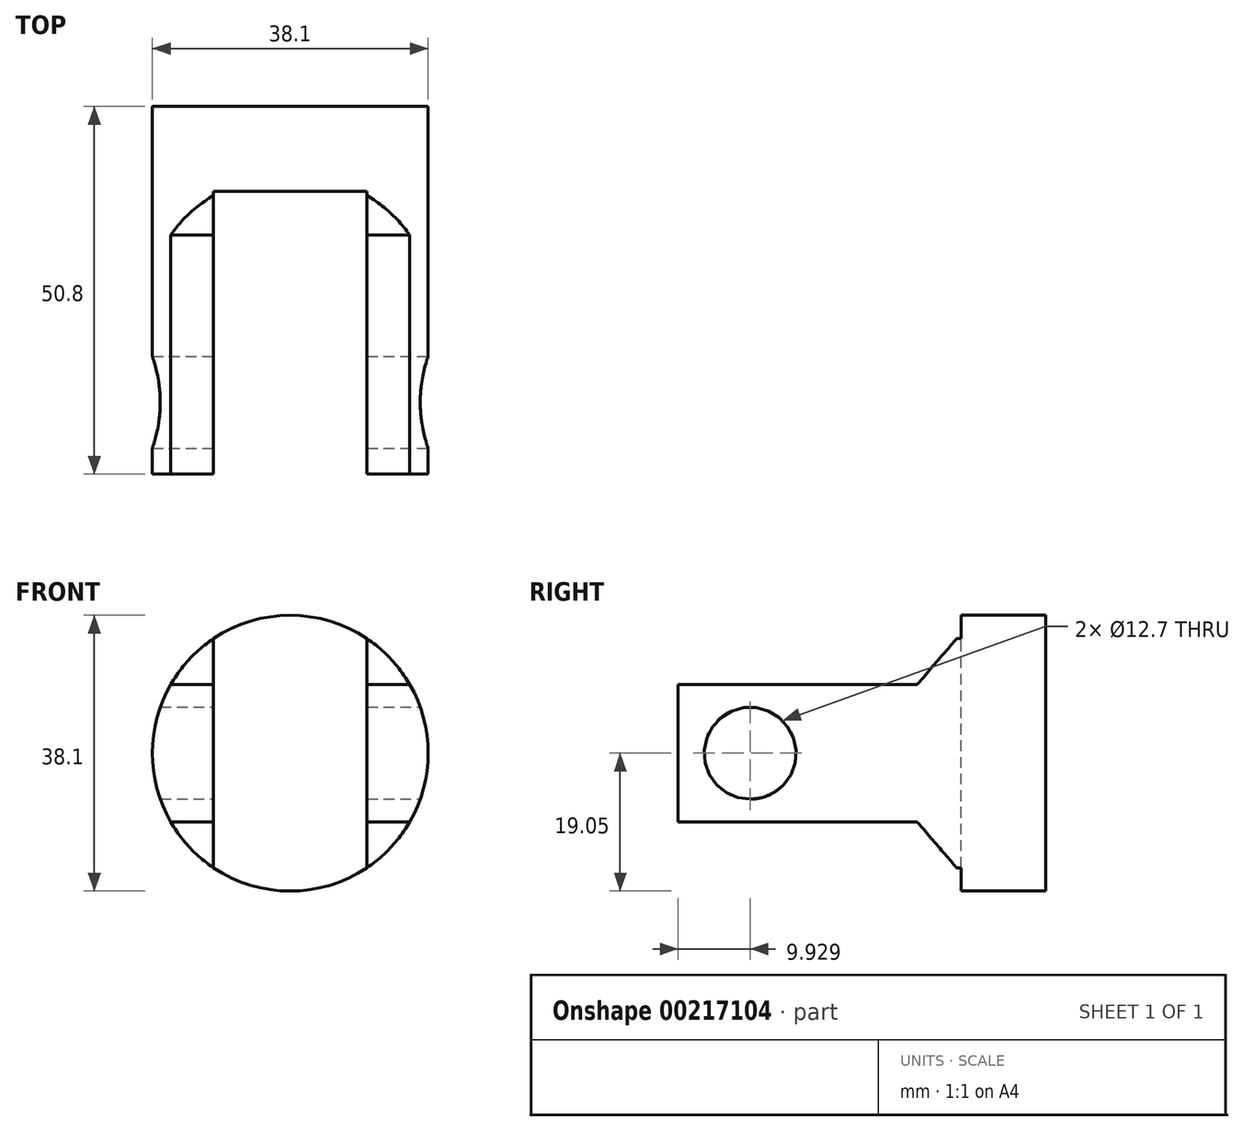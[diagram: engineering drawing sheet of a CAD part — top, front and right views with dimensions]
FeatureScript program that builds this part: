
annotation { "Feature Type Name" : "Feature", "Feature Type Description" : "" }
export const myFeature = defineFeature(function(context is Context, id is Id, definition is map)
    precondition{}
    {
        {
            var Q0;
            Q0=qCreatedBy(makeId("Front.planeOp"),FACE);
            var sketch = newSketch(context, id + "F0", { "sketchPlane" : qUnion([Q0])});
            skCircle(sketch, "E0", {"center": v(0, 0) * mm, "radius": 19.05 * mm});
            skSolve(sketch);
        }
        {
            var Q0;
            Q0 = qSketchRegion(id + "F0", true);
            extrude(context, id + "F1", {"entities" : qUnion([Q0]), "depth" : 50.8 * mm});
        }
        {
            var Q0;
            Q0=qCreatedBy(makeId("Top.planeOp"),FACE);
            var sketch = newSketch(context, id + "F2", { "sketchPlane" : qUnion([Q0])});
            skLineSegment(sketch, "E1.bottom", {"start": v(10.6, -90.36) * mm, "end": v(-10.6, -90.36) * mm});
            skLineSegment(sketch, "E1.top", {"start": v(10.6, -11.7) * mm, "end": v(-10.6, -11.7) * mm});
            skLineSegment(sketch, "E1.left", {"start": v(10.6, -90.36) * mm, "end": v(10.6, -11.7) * mm});
            skLineSegment(sketch, "E1.right", {"start": v(-10.6, -90.36) * mm, "end": v(-10.6, -11.7) * mm});
            skPoint(sketch, "E1.middle", {"position": v(0, -51.03) * mm});
            skSolve(sketch);
        }
        {
            var Q0;
            Q0 = qSketchRegion(id + "F2", true);
            extrude(context, id + "F3", {"entities" : qUnion([Q0]), "operationType" : NewBodyOperationType.REMOVE, "oppositeDirection" : true, "depth" : 76.2 * mm, "symmetric" : true});
        }
        {
            var Q0;
            Q0=qCreatedBy(makeId("Right.planeOp"),FACE);
            var sketch = newSketch(context, id + "F4", { "sketchPlane" : qUnion([Q0])});
            skCircle(sketch, "E2", {"center": v(-40.87, 0) * mm, "radius": 6.35 * mm});
            skLineSegment(sketch, "E3", {"start": v(-54.9, 0) * mm, "end": v(-54.9, -9.5) * mm});
            skLineSegment(sketch, "E4", {"start": v(-54.9, -9.5) * mm, "end": v(-17.78, -9.5) * mm});
            skLineSegment(sketch, "E5", {"start": v(-17.78, -9.5) * mm, "end": v(-12.26, -15.9) * mm});
            skLineSegment(sketch, "E6", {"start": v(-12.26, -15.9) * mm, "end": v(-18.89, -28.72) * mm});
            skLineSegment(sketch, "E7", {"start": v(-18.89, -28.72) * mm, "end": v(-61.3, -20.33) * mm});
            skLineSegment(sketch, "E8", {"start": v(-61.3, -20.33) * mm, "end": v(-54.9, -9.5) * mm});
            skLineSegment(sketch, "E9.MirrorCS", {"start": v(-54.9, 9.5) * mm, "end": v(-17.78, 9.5) * mm});
            skLineSegment(sketch, "E10.MirrorCS", {"start": v(-61.3, 20.33) * mm, "end": v(-54.9, 9.5) * mm});
            skLineSegment(sketch, "E11.MirrorCS", {"start": v(-18.89, 28.72) * mm, "end": v(-61.3, 20.33) * mm});
            skLineSegment(sketch, "E12.MirrorCS", {"start": v(-12.26, 15.9) * mm, "end": v(-18.89, 28.72) * mm});
            skLineSegment(sketch, "E13.MirrorCS", {"start": v(-17.78, 9.5) * mm, "end": v(-12.26, 15.9) * mm});
            skSolve(sketch);
        }
        {
            var Q0;
            Q0=makeQuery(id+"F4.imprint","IMPRINT",FACE,{"disambiguationData":[TD([[makeQuery(id+"F4.imprint","IMPRINT",EDGE,{"derivedFrom":sQuery(id+"F4.wireOp",EDGE,"E2")}),1.0]])]});
            var Q1;
            Q1=makeQuery(id+"F4.imprint","IMPRINT",FACE,{"disambiguationData":[TD([[makeQuery(id+"F4.imprint","IMPRINT",EDGE,{"derivedFrom":sQuery(id+"F4.wireOp",EDGE,"E4")}),-1.0]])]});
            var Q2;
            Q2=makeQuery(id+"F4.imprint","IMPRINT",FACE,{"disambiguationData":[TD([[makeQuery(id+"F4.imprint","IMPRINT",EDGE,{"derivedFrom":sQuery(id+"F4.wireOp",EDGE,"E9.MirrorCS")}),1.0]])]});
            extrude(context, id + "F5", {"entities" : qUnion([Q0, Q1, Q2]), "operationType" : NewBodyOperationType.REMOVE, "oppositeDirection" : true, "depth" : 76.2 * mm, "symmetric" : true});
        }
    });
